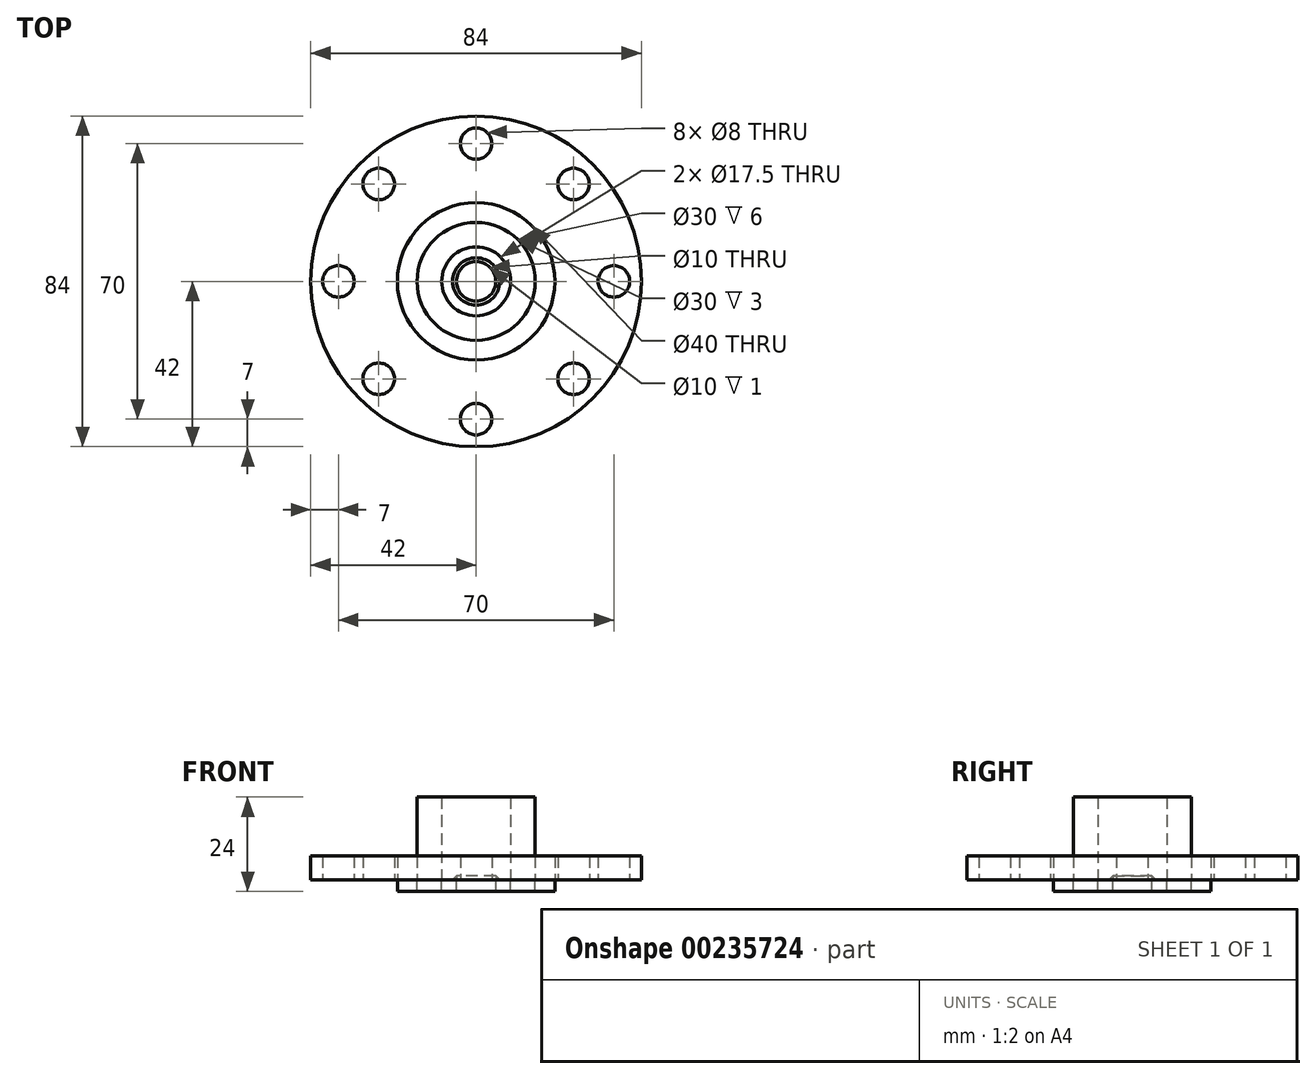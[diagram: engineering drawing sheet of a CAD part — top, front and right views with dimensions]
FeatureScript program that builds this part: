
annotation { "Feature Type Name" : "Feature", "Feature Type Description" : "" }
export const myFeature = defineFeature(function(context is Context, id is Id, definition is map)
    precondition{}
    {
        {
            var Q0;
            Q0=qCreatedBy(makeId("Top.planeOp"),FACE);
            var sketch = newSketch(context, id + "F0", { "sketchPlane" : qUnion([Q0])});
            skCircle(sketch, "E0", {"center": v(0, 0) * mm, "radius": 42 * mm});
            skCircle(sketch, "E1", {"center": v(0, 0) * mm, "radius": 35 * mm, "construction": true});
            skCircle(sketch, "E2", {"center": v(0, 0) * mm, "radius": 20 * mm});
            skCircle(sketch, "E3", {"center": v(0, 0) * mm, "radius": 5 * mm});
            skCircle(sketch, "E4", {"center": v(0, 0) * mm, "radius": 8.75 * mm});
            skLineSegment(sketch, "E5", {"start": v(0, 0) * mm, "end": v(0, 42) * mm, "construction": true});
            skCircle(sketch, "E6", {"center": v(0, 0) * mm, "radius": 15 * mm});
            skCircle(sketch, "E7", {"center": v(0, 35) * mm, "radius": 4 * mm});
            skCircle(sketch, "E8.1.0", {"center": v(-24.75, 24.75) * mm, "radius": 4 * mm});
            skCircle(sketch, "E8.2.0", {"center": v(-35, 0) * mm, "radius": 4 * mm});
            skCircle(sketch, "E9.1.3.0", {"center": v(-24.75, -24.75) * mm, "radius": 4 * mm});
            skCircle(sketch, "E9.1.4.0", {"center": v(0, -35) * mm, "radius": 4 * mm});
            skCircle(sketch, "E9.1.5.0", {"center": v(24.75, -24.75) * mm, "radius": 4 * mm});
            skCircle(sketch, "E9.1.6.0", {"center": v(35, 0) * mm, "radius": 4 * mm});
            skCircle(sketch, "E9.1.7.0", {"center": v(24.75, 24.75) * mm, "radius": 4 * mm});
            skLineSegment(sketch, "E10", {"start": v(0, 0) * mm, "end": v(24.75, 24.75) * mm, "construction": true});
            skSolve(sketch);
        }
        {
            var Q0;
            Q0=makeQuery(id+"F0.imprint","IMPRINT",FACE,{"disambiguationData":[TD([[makeQuery(id+"F0.imprint","IMPRINT",EDGE,{"derivedFrom":sQuery(id+"F0.wireOp",EDGE,"E4")}),-1.0]])]});
            extrude(context, id + "F1", {"entities" : qUnion([Q0]), "depth" : 21 * mm});
        }
        {
            var Q0;
            Q0=makeQuery(id+"F0.imprint","IMPRINT",FACE,{"disambiguationData":[TD([[makeQuery(id+"F0.imprint","IMPRINT",EDGE,{"derivedFrom":sQuery(id+"F0.wireOp",EDGE,"E2")}),1.0]])]});
            extrude(context, id + "F2", {"entities" : qUnion([Q0]), "oppositeDirection" : true, "depth" : 3 * mm});
        }
        {
            var Q0;
            Q0=makeQuery(id+"F0.imprint","IMPRINT",FACE,{"disambiguationData":[TD([[makeQuery(id+"F0.imprint","IMPRINT",EDGE,{"derivedFrom":sQuery(id+"F0.wireOp",EDGE,"E0")}),1.0]])]});
            extrude(context, id + "F3", {"entities" : qUnion([Q0]), "depth" : 6 * mm});
        }
        {
            var Q0;
            Q0=makeQuery(id+"F0.imprint","IMPRINT",FACE,{"disambiguationData":[TD([[makeQuery(id+"F0.imprint","IMPRINT",EDGE,{"derivedFrom":sQuery(id+"F0.wireOp",EDGE,"E2")}),1.0]])]});
            extrude(context, id + "F4", {"entities" : qUnion([Q0]), "depth" : 6 * mm});
        }
        {
            var Q0;
            Q0=makeQuery(id+"F0.imprint","IMPRINT",FACE,{"disambiguationData":[TD([[makeQuery(id+"F0.imprint","IMPRINT",EDGE,{"derivedFrom":sQuery(id+"F0.wireOp",EDGE,"E3")}),-1.0]])]});
            extrude(context, id + "F5", {"entities" : qUnion([Q0]), "operationType" : NewBodyOperationType.ADD, "oppositeDirection" : true, "depth" : 3 * mm});
        }
        {
            var Q0;
            Q0=makeQuery(id+"F0.imprint","IMPRINT",FACE,{"disambiguationData":[TD([[makeQuery(id+"F0.imprint","IMPRINT",EDGE,{"derivedFrom":sQuery(id+"F0.wireOp",EDGE,"E4")}),-1.0]])]});
            extrude(context, id + "F6", {"entities" : qUnion([Q0]), "oppositeDirection" : true, "depth" : 3 * mm});
        }
        {
            var Q0;
            Q0=makeQuery(id+"F0.imprint","IMPRINT",FACE,{"disambiguationData":[TD([[makeQuery(id+"F0.imprint","IMPRINT",EDGE,{"derivedFrom":sQuery(id+"F0.wireOp",EDGE,"E3")}),-1.0]])]});
            extrude(context, id + "F7", {"entities" : qUnion([Q0]), "depth" : 1 * mm});
        }
        {
            var Q0;
            Q0=makeQuery(id+"F7.opExtrude","CAP_EDGE",EDGE,{"disambiguationData":[OSD([sQuery(id+"F0.wireOp",EDGE,"E4")])],"isStart":false});
            chamfer(context, id + "F8", {"entities" : qUnion([Q0]), "width" : 3.75 * mm, "tangentPropagation" : true});
        }
    });
